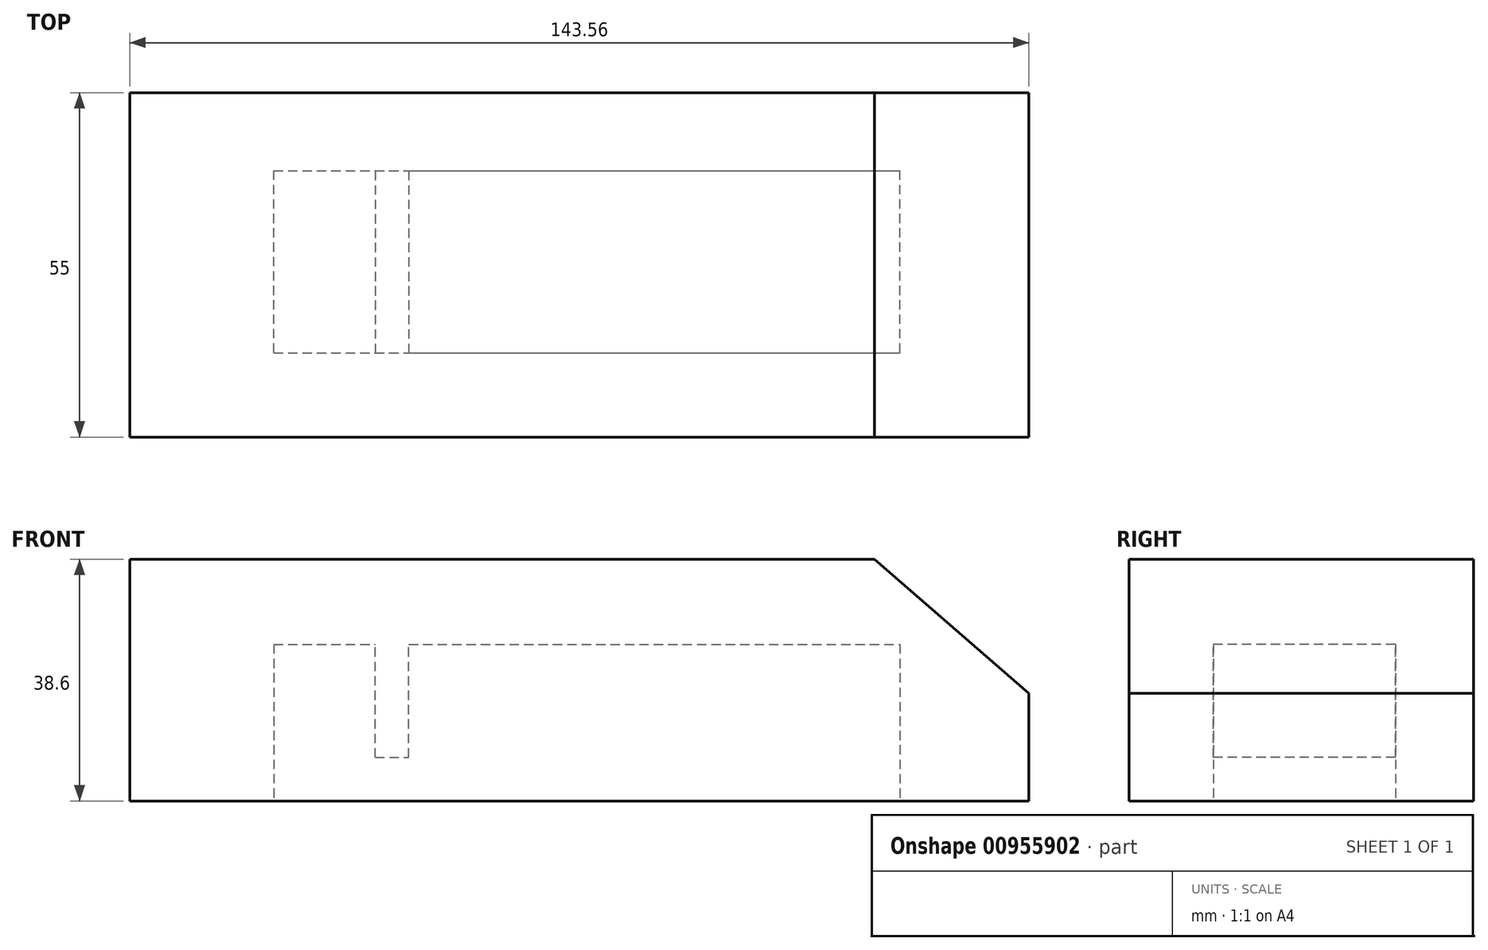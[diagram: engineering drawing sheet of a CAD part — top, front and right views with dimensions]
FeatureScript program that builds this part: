
annotation { "Feature Type Name" : "Feature", "Feature Type Description" : "" }
export const myFeature = defineFeature(function(context is Context, id is Id, definition is map)
    precondition{}
    {
        {
            var Q0;
            Q0=qCreatedBy(makeId("Front.planeOp"),FACE);
            var sketch = newSketch(context, id + "F0", { "sketchPlane" : qUnion([Q0])});
            skLineSegment(sketch, "E0", {"start": v(66.69, -30.57) * mm, "end": v(-76.87, -30.57) * mm});
            skLineSegment(sketch, "E1", {"start": v(-76.87, -30.57) * mm, "end": v(-76.87, 8.03) * mm});
            skLineSegment(sketch, "E2", {"start": v(-76.87, 8.03) * mm, "end": v(42.05, 8.03) * mm});
            skLineSegment(sketch, "E3", {"start": v(42.05, 8.03) * mm, "end": v(66.69, -13.4) * mm});
            skLineSegment(sketch, "E4", {"start": v(66.69, -13.4) * mm, "end": v(66.69, -30.57) * mm});
            skSolve(sketch);
        }
        {
            var Q0;
            Q0 = qSketchRegion(id + "F0", true);
            extrude(context, id + "F1", {"entities" : qUnion([Q0]), "depth" : 55 * mm, "offsetDistance" : 25 * mm});
        }
        {
            var Q0;
            Q0=makeQuery(id+"F1.opExtrude","SWEPT_FACE",FACE,{"disambiguationData":[OSD([sQuery(id+"F0.wireOp",EDGE,"E0")])]});
            var sketch = newSketch(context, id + "F2", { "sketchPlane" : qUnion([Q0])});
            skLineSegment(sketch, "E5.bottom", {"start": v(-53.88, 41.53) * mm, "end": v(46.12, 41.53) * mm});
            skLineSegment(sketch, "E5.top", {"start": v(-53.88, 12.5) * mm, "end": v(46.12, 12.5) * mm});
            skLineSegment(sketch, "E5.left", {"start": v(-53.88, 41.53) * mm, "end": v(-53.88, 12.5) * mm});
            skLineSegment(sketch, "E5.right", {"start": v(46.12, 41.53) * mm, "end": v(46.12, 12.5) * mm});
            skSolve(sketch);
        }
        {
            var Q0;
            Q0 = qSketchRegion(id + "F2", true);
            extrude(context, id + "F3", {"entities" : qUnion([Q0]), "operationType" : NewBodyOperationType.REMOVE, "oppositeDirection" : true, "depth" : 25 * mm, "offsetDistance" : 25 * mm});
        }
        {
            var Q0;
            Q0=makeQuery(id+"F3.boolean.opBoolean","COPY",FACE,{"derivedFrom":makeQuery(id+"F3.opExtrude","SWEPT_FACE",FACE,{"disambiguationData":[OSD([sQuery(id+"F2.wireOp",EDGE,"E5.bottom")])]})});
            var sketch = newSketch(context, id + "F4", { "sketchPlane" : qUnion([Q0])});
            skLineSegment(sketch, "E6.bottom", {"start": v(37.68, -23.64) * mm, "end": v(32.3, -23.64) * mm});
            skLineSegment(sketch, "E6.top", {"start": v(37.68, -5.57) * mm, "end": v(32.3, -5.57) * mm});
            skLineSegment(sketch, "E6.left", {"start": v(37.68, -23.64) * mm, "end": v(37.68, -5.57) * mm});
            skLineSegment(sketch, "E6.right", {"start": v(32.3, -23.64) * mm, "end": v(32.3, -5.57) * mm});
            skSolve(sketch);
        }
        {
            var Q0;
            Q0 = qSketchRegion(id + "F4", true);
            extrude(context, id + "F5", {"entities" : qUnion([Q0]), "operationType" : NewBodyOperationType.ADD, "endBound" : BoundingType.UP_TO_NEXT, "depth" : 25 * mm, "offsetDistance" : 25 * mm});
        }
    });
